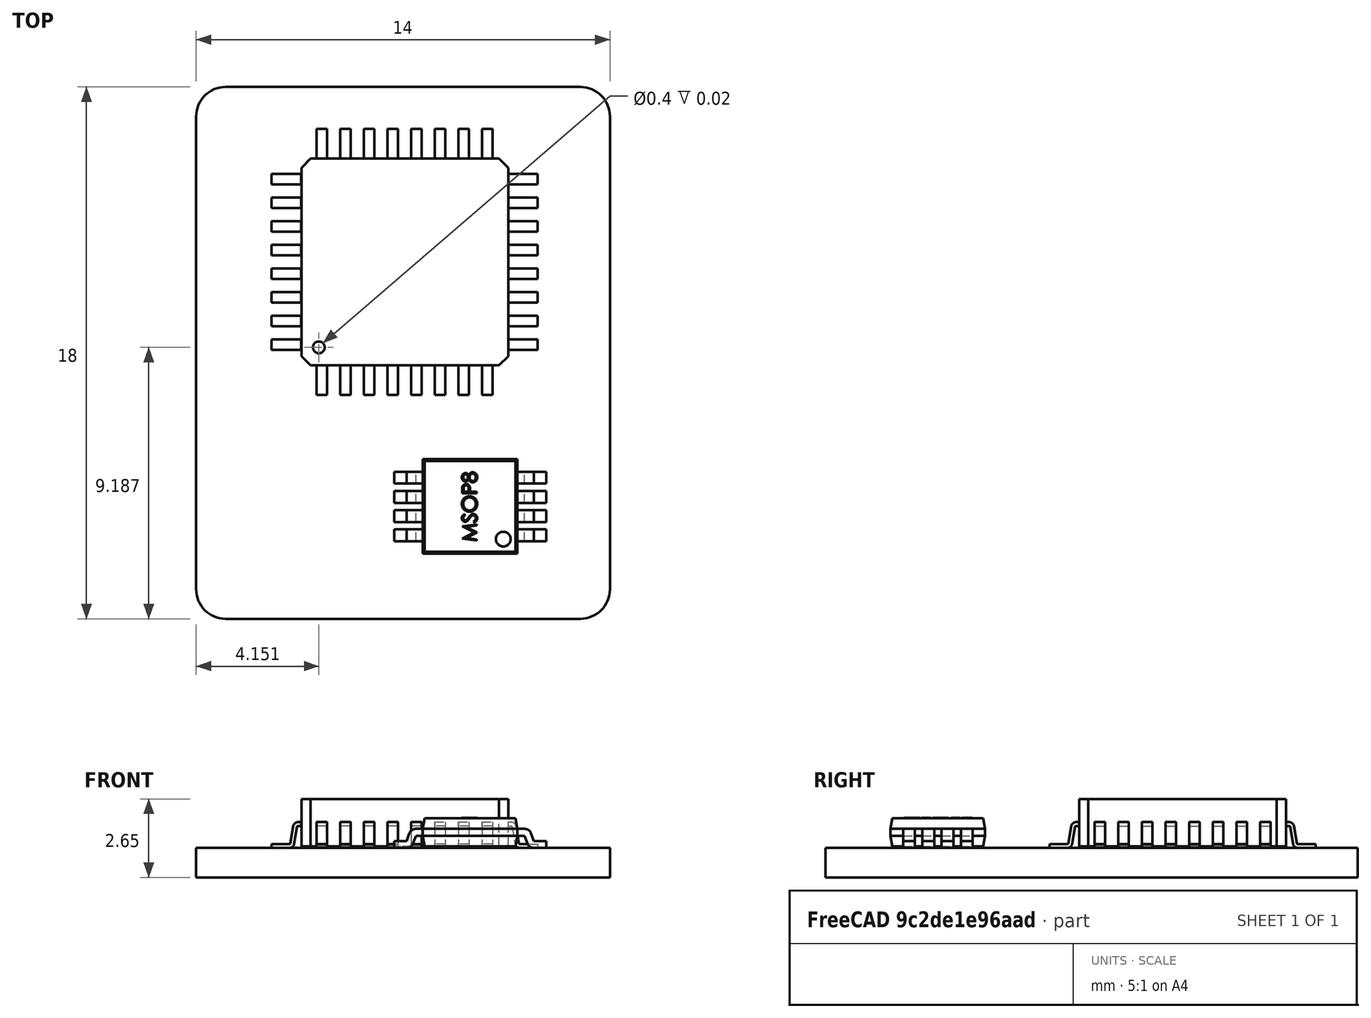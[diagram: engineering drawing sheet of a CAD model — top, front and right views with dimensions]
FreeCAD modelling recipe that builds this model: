
FCSTD DOCUMENT  (FreeCAD 0.16R6703 (Git))
Label: fpga-config-memory
License: All rights reserved
LicenseURL: http://en.wikipedia.org/wiki/All_rights_reserved
objects: Part::Feature×1, Part::Compound×1, Part::Part2DObjectPython×1, Part::Extrusion×1
note: 4 computed .brp shape members not serialized (recipe doc carries the construction recipe); baked Part::Feature solids carry a one-line shape summary decoded from their .brp

FEATURE [Part::Feature] Part__Feature355  label="User_Library-MSOP8-2"
  Placement = pos=(4.27511,4.79953,1) rot=(0.57735,0.57735,0.57735;2.0944rad)
  shape: bbox 5.15 x 3.2 x 1.01 mm, 191 faces (baked)
FEATURE [Part::Compound] Compound020  label="PQFP-034"
  Placement = pos=(-2.46873,8.58698,1.05463) rot=(0,0,1;0rad)
FEATURE [Part::Part2DObjectPython] Rectangle  # Draft 2D object (typed FeaturePython)
  ChamferSize = 0
  Columns = 1
  FilletRadius = 1
  Height = -18
  Length = 14
  MakeFace = true
  Placement = pos=(-5,19,0) rot=(0,0,1;0rad)
  Rows = 1
  Support = -> Compound020
FEATURE [Part::Extrusion] Extrude
  Base = -> Rectangle
  Dir = (0,0,1)
  Solid = false
